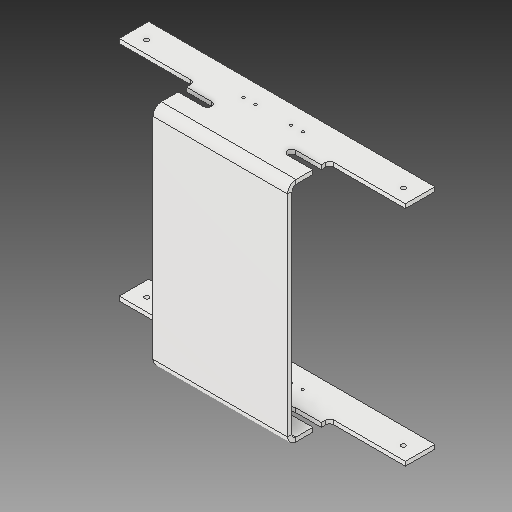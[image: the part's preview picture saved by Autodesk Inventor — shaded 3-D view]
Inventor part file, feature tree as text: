
AUTODESK INVENTOR PART (.ipt)
format: ipt  version: 2018 (Build 220112000, 112)  size: 135,168 bytes
history: native  units: in
note: dims shown in document units (in); Inventor stores cm internally (conversion verified against a paired STEP export)
features: fillet x1
ambient origin geometry x8: Origin, YZ Plane, XZ Plane, XY Plane, X Axis, Y Axis, Z Axis, Center Point
bodies: Solid1 (feature_tree)
feature tree (1):
  fillet  "Fillet2"  [1 undecoded]
note: 1 required parameter value undecoded (feature->parameter linkage not recoverable at this tier; creation-order binding heuristic only, values carry confidence <= 0.55)
